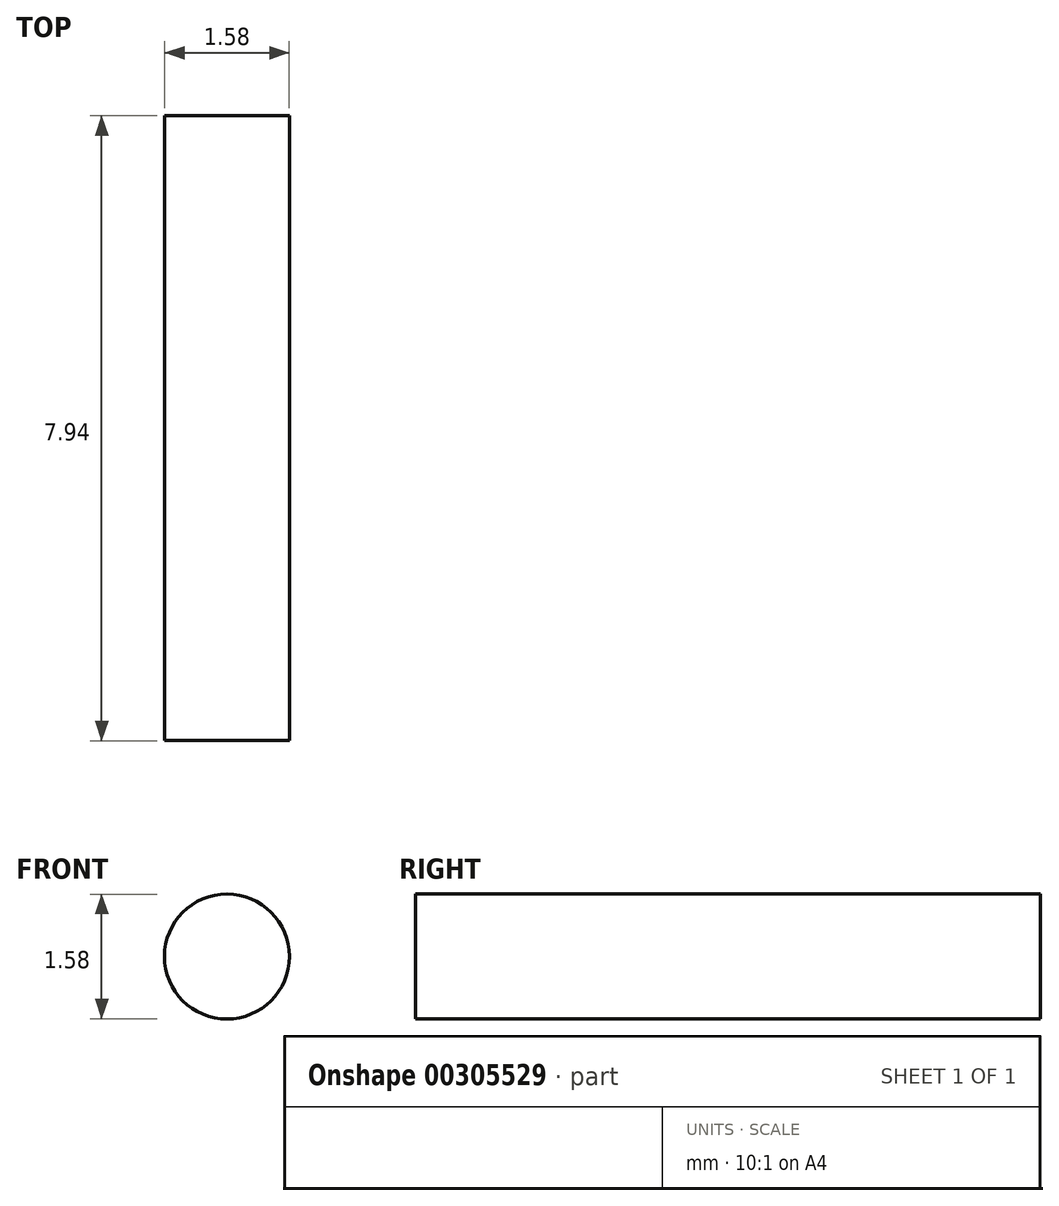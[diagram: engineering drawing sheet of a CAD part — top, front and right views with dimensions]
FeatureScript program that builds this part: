
annotation { "Feature Type Name" : "Feature", "Feature Type Description" : "" }
export const myFeature = defineFeature(function(context is Context, id is Id, definition is map)
    precondition{}
    {
        {
            var Q0;
            Q0=qCreatedBy(makeId("Front.planeOp"),FACE);
            var sketch = newSketch(context, id + "F0", { "sketchPlane" : qUnion([Q0])});
            skCircle(sketch, "E0", {"center": v(0, 0) * mm, "radius": 0.8 * mm});
            skSolve(sketch);
        }
        {
            var Q0;
            Q0=makeQuery(id+"F0.imprint","IMPRINT",FACE,{"disambiguationData":[TD([[makeQuery(id+"F0.imprint","IMPRINT",EDGE,{"derivedFrom":sQuery(id+"F0.wireOp",EDGE,"E0")}),1.0]])]});
            extrude(context, id + "F1", {"entities" : qUnion([Q0]), "depth" : 7.94 * mm});
        }
    });
